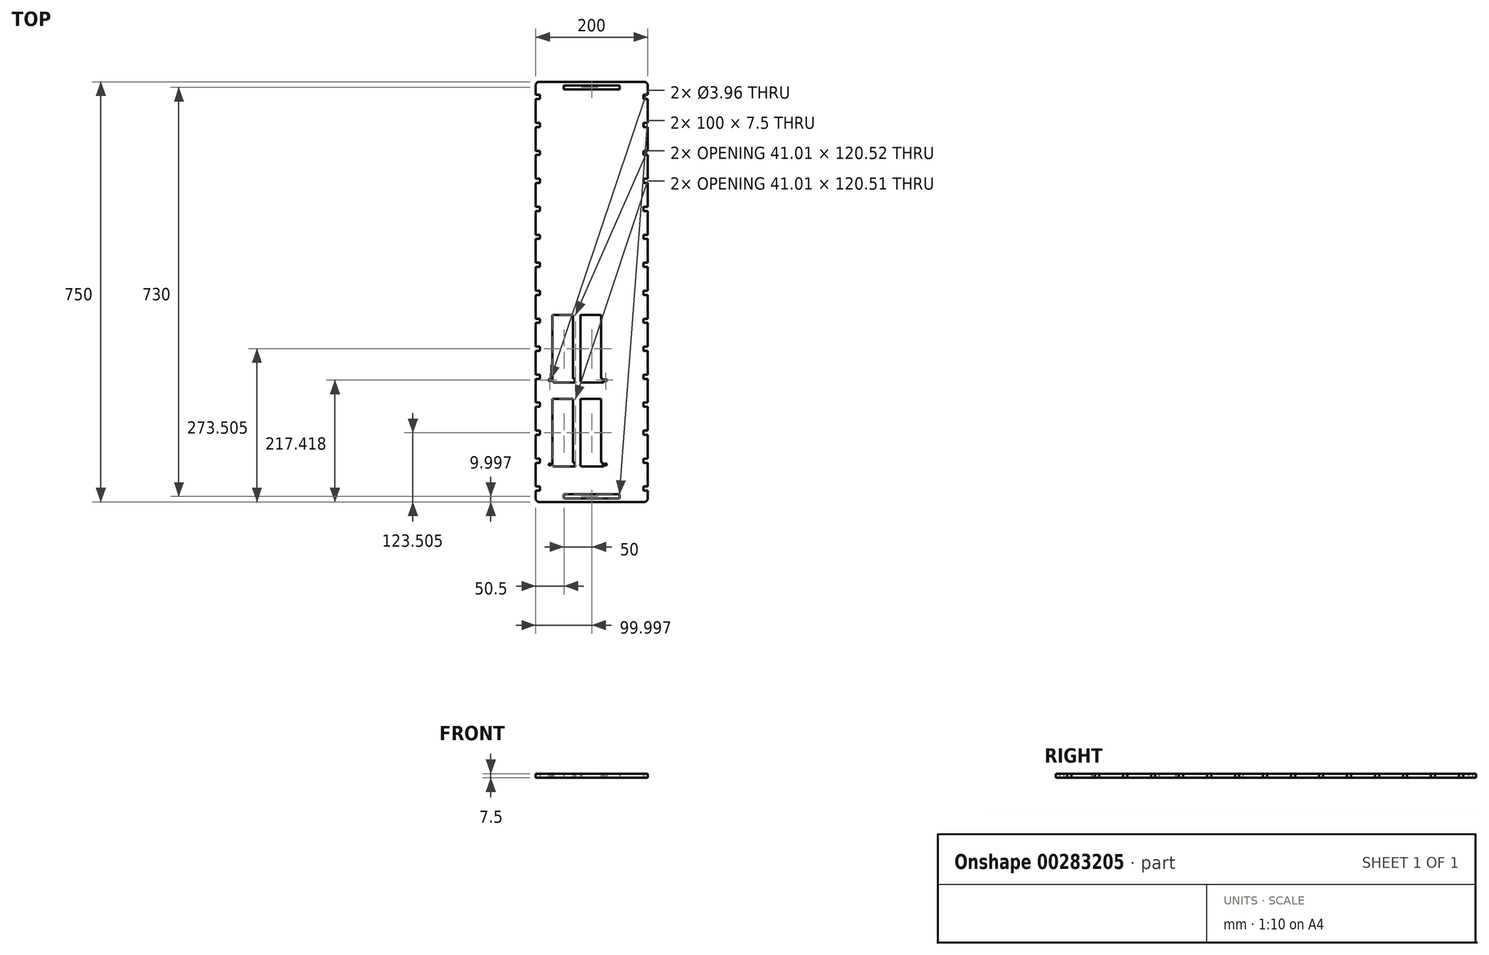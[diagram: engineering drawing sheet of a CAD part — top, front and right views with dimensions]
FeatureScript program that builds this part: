
annotation { "Feature Type Name" : "Feature", "Feature Type Description" : "" }
export const myFeature = defineFeature(function(context is Context, id is Id, definition is map)
    precondition{}
    {
        {
            var Q0;
            Q0=qCreatedBy(makeId("Top.planeOp"),FACE);
            var sketch = newSketch(context, id + "F0", { "sketchPlane" : qUnion([Q0])});
            skLineSegment(sketch, "E0.bottom", {"start": v(-77.83, 397.38) * mm, "end": v(109.47, 397.38) * mm});
            skLineSegment(sketch, "E0.top", {"start": v(-77.83, -352.62) * mm, "end": v(109.47, -352.62) * mm});
            skLineSegment(sketch, "E0.left", {"start": v(-84.18, 391.03) * mm, "end": v(-84.18, 374.07) * mm});
            skLineSegment(sketch, "E0.right", {"start": v(115.82, 391.03) * mm, "end": v(115.82, 374.18) * mm});
            skLineSegment(sketch, "E1", {"start": v(15.82, -352.62) * mm, "end": v(15.82, -332.62) * mm, "construction": true});
            skPoint(sketch, "E1.endSnap0", {"position": v(15.82, -352.62) * mm});
            skLineSegment(sketch, "E2", {"start": v(-84.18, 374.07) * mm, "end": v(-59.18, 374.07) * mm, "construction": true});
            skLineSegment(sketch, "E3", {"start": v(15.82, 397.38) * mm, "end": v(15.82, 377.38) * mm, "construction": true});
            skPoint(sketch, "E3.endSnap0", {"position": v(15.82, 397.38) * mm});
            skPoint(sketch, "E4.visualSharp", {"position": v(-84.18, 397.38) * mm});
            skArc(sketch, "E4.filletArc", {"start": v(-77.83, 397.38) * mm, "mid": v(-82.32, 395.52) * mm, "end": v(-84.18, 391.03) * mm});
            skPoint(sketch, "E5.visualSharp", {"position": v(115.82, 397.38) * mm});
            skArc(sketch, "E5.filletArc", {"start": v(115.82, 391.03) * mm, "mid": v(113.96, 395.52) * mm, "end": v(109.47, 397.38) * mm});
            skPoint(sketch, "E6.visualSharp", {"position": v(115.82, -352.62) * mm});
            skArc(sketch, "E6.filletArc", {"start": v(109.47, -352.62) * mm, "mid": v(113.96, -350.76) * mm, "end": v(115.82, -346.27) * mm});
            skPoint(sketch, "E7.visualSharp", {"position": v(-84.18, -352.62) * mm});
            skArc(sketch, "E7.filletArc", {"start": v(-84.18, -346.27) * mm, "mid": v(-82.32, -350.76) * mm, "end": v(-77.83, -352.62) * mm});
            skLineSegment(sketch, "E8.bottom", {"start": v(-84.18, -332.62) * mm, "end": v(-76.68, -332.62) * mm});
            skLineSegment(sketch, "E8.top", {"start": v(-84.18, -325.12) * mm, "end": v(-76.68, -325.12) * mm});
            skLineSegment(sketch, "E8.right", {"start": v(-76.68, -332.62) * mm, "end": v(-76.68, -325.12) * mm});
            skLineSegment(sketch, "E9.0.1.0", {"start": v(-84.18, -275.17) * mm, "end": v(-76.68, -275.17) * mm});
            skLineSegment(sketch, "E9.0.1.1", {"start": v(-84.18, -282.67) * mm, "end": v(-76.68, -282.67) * mm});
            skLineSegment(sketch, "E9.0.1.3", {"start": v(-76.68, -282.67) * mm, "end": v(-76.68, -275.17) * mm});
            skLineSegment(sketch, "E9.0.2.0", {"start": v(-84.18, -225.22) * mm, "end": v(-76.68, -225.22) * mm});
            skLineSegment(sketch, "E9.0.2.1", {"start": v(-84.18, -232.72) * mm, "end": v(-76.68, -232.72) * mm});
            skLineSegment(sketch, "E9.0.2.3", {"start": v(-76.68, -232.72) * mm, "end": v(-76.68, -225.22) * mm});
            skLineSegment(sketch, "E9.0.3.0", {"start": v(-84.18, -175.27) * mm, "end": v(-76.68, -175.27) * mm});
            skLineSegment(sketch, "E9.0.3.1", {"start": v(-84.18, -182.77) * mm, "end": v(-76.68, -182.77) * mm});
            skLineSegment(sketch, "E9.0.3.3", {"start": v(-76.68, -182.77) * mm, "end": v(-76.68, -175.27) * mm});
            skLineSegment(sketch, "E9.0.4.0", {"start": v(-84.18, -125.32) * mm, "end": v(-76.68, -125.32) * mm});
            skLineSegment(sketch, "E9.0.4.1", {"start": v(-84.18, -132.82) * mm, "end": v(-76.68, -132.82) * mm});
            skLineSegment(sketch, "E9.0.4.3", {"start": v(-76.68, -132.82) * mm, "end": v(-76.68, -125.32) * mm});
            skLineSegment(sketch, "E9.0.5.0", {"start": v(-84.18, -75.37) * mm, "end": v(-76.68, -75.37) * mm});
            skLineSegment(sketch, "E9.0.5.1", {"start": v(-84.18, -82.87) * mm, "end": v(-76.68, -82.87) * mm});
            skLineSegment(sketch, "E9.0.5.3", {"start": v(-76.68, -82.87) * mm, "end": v(-76.68, -75.37) * mm});
            skLineSegment(sketch, "E9.0.6.0", {"start": v(-84.18, -25.42) * mm, "end": v(-76.68, -25.42) * mm});
            skLineSegment(sketch, "E9.0.6.1", {"start": v(-84.18, -32.92) * mm, "end": v(-76.68, -32.92) * mm});
            skLineSegment(sketch, "E9.0.6.3", {"start": v(-76.68, -32.92) * mm, "end": v(-76.68, -25.42) * mm});
            skLineSegment(sketch, "E9.0.7.0", {"start": v(-84.18, 24.53) * mm, "end": v(-76.68, 24.53) * mm});
            skLineSegment(sketch, "E9.0.7.1", {"start": v(-84.18, 17.03) * mm, "end": v(-76.68, 17.03) * mm});
            skLineSegment(sketch, "E9.0.7.3", {"start": v(-76.68, 17.03) * mm, "end": v(-76.68, 24.53) * mm});
            skLineSegment(sketch, "E9.0.8.0", {"start": v(-84.18, 74.48) * mm, "end": v(-76.68, 74.48) * mm});
            skLineSegment(sketch, "E9.0.8.1", {"start": v(-84.18, 66.98) * mm, "end": v(-76.68, 66.98) * mm});
            skLineSegment(sketch, "E9.0.8.3", {"start": v(-76.68, 66.98) * mm, "end": v(-76.68, 74.48) * mm});
            skLineSegment(sketch, "E9.0.9.0", {"start": v(-84.18, 124.43) * mm, "end": v(-76.68, 124.43) * mm});
            skLineSegment(sketch, "E9.0.9.1", {"start": v(-84.18, 116.93) * mm, "end": v(-76.68, 116.93) * mm});
            skLineSegment(sketch, "E9.0.9.3", {"start": v(-76.68, 116.93) * mm, "end": v(-76.68, 124.43) * mm});
            skLineSegment(sketch, "E9.0.10.0", {"start": v(-84.18, 174.38) * mm, "end": v(-76.68, 174.38) * mm});
            skLineSegment(sketch, "E9.0.10.1", {"start": v(-84.18, 166.88) * mm, "end": v(-76.68, 166.88) * mm});
            skLineSegment(sketch, "E9.0.10.3", {"start": v(-76.68, 166.88) * mm, "end": v(-76.68, 174.38) * mm});
            skLineSegment(sketch, "E9.0.11.0", {"start": v(-84.18, 224.33) * mm, "end": v(-76.68, 224.33) * mm});
            skLineSegment(sketch, "E9.0.11.1", {"start": v(-84.18, 216.83) * mm, "end": v(-76.68, 216.83) * mm});
            skLineSegment(sketch, "E9.0.11.3", {"start": v(-76.68, 216.83) * mm, "end": v(-76.68, 224.33) * mm});
            skLineSegment(sketch, "E9.0.12.0", {"start": v(-84.18, 274.28) * mm, "end": v(-76.68, 274.28) * mm});
            skLineSegment(sketch, "E9.0.12.1", {"start": v(-84.18, 266.78) * mm, "end": v(-76.68, 266.78) * mm});
            skLineSegment(sketch, "E9.0.12.3", {"start": v(-76.68, 266.78) * mm, "end": v(-76.68, 274.28) * mm});
            skLineSegment(sketch, "E9.0.13.0", {"start": v(-84.18, 324.23) * mm, "end": v(-76.68, 324.23) * mm});
            skLineSegment(sketch, "E9.0.13.1", {"start": v(-84.18, 316.73) * mm, "end": v(-76.68, 316.73) * mm});
            skLineSegment(sketch, "E9.0.13.3", {"start": v(-76.68, 316.73) * mm, "end": v(-76.68, 324.23) * mm});
            skLineSegment(sketch, "E9.0.14.0", {"start": v(-84.18, 374.18) * mm, "end": v(-76.68, 374.18) * mm});
            skLineSegment(sketch, "E9.0.14.1", {"start": v(-84.18, 366.68) * mm, "end": v(-76.68, 366.68) * mm});
            skLineSegment(sketch, "E9.0.14.2", {"start": v(-84.18, 374.07) * mm, "end": v(-84.18, 374.18) * mm});
            skLineSegment(sketch, "E9.0.14.3", {"start": v(-76.68, 366.68) * mm, "end": v(-76.68, 374.18) * mm});
            skLineSegment(sketch, "E9.direction1", {"start": v(-84.18, -332.62) * mm, "end": v(-58.78, -332.62) * mm, "construction": true});
            skLineSegment(sketch, "E9.direction2", {"start": v(-84.18, -325.12) * mm, "end": v(-84.18, -282.67) * mm, "construction": true});
            skLineSegment(sketch, "E10.bottom", {"start": v(115.82, -332.62) * mm, "end": v(108.32, -332.62) * mm});
            skLineSegment(sketch, "E10.top", {"start": v(115.82, -325.12) * mm, "end": v(108.32, -325.12) * mm});
            skLineSegment(sketch, "E10.right", {"start": v(108.32, -332.62) * mm, "end": v(108.32, -325.12) * mm});
            skLineSegment(sketch, "E11.0.1.0", {"start": v(115.82, -282.67) * mm, "end": v(108.32, -282.67) * mm});
            skLineSegment(sketch, "E11.0.1.2", {"start": v(115.82, -275.17) * mm, "end": v(108.32, -275.17) * mm});
            skLineSegment(sketch, "E11.0.1.3", {"start": v(108.32, -282.67) * mm, "end": v(108.32, -275.17) * mm});
            skLineSegment(sketch, "E11.0.2.0", {"start": v(115.82, -232.72) * mm, "end": v(108.32, -232.72) * mm});
            skLineSegment(sketch, "E11.0.2.2", {"start": v(115.82, -225.22) * mm, "end": v(108.32, -225.22) * mm});
            skLineSegment(sketch, "E11.0.2.3", {"start": v(108.32, -232.72) * mm, "end": v(108.32, -225.22) * mm});
            skLineSegment(sketch, "E11.0.3.0", {"start": v(115.82, -182.77) * mm, "end": v(108.32, -182.77) * mm});
            skLineSegment(sketch, "E11.0.3.2", {"start": v(115.82, -175.27) * mm, "end": v(108.32, -175.27) * mm});
            skLineSegment(sketch, "E11.0.3.3", {"start": v(108.32, -182.77) * mm, "end": v(108.32, -175.27) * mm});
            skLineSegment(sketch, "E11.0.4.0", {"start": v(115.82, -132.82) * mm, "end": v(108.32, -132.82) * mm});
            skLineSegment(sketch, "E11.0.4.2", {"start": v(115.82, -125.32) * mm, "end": v(108.32, -125.32) * mm});
            skLineSegment(sketch, "E11.0.4.3", {"start": v(108.32, -132.82) * mm, "end": v(108.32, -125.32) * mm});
            skLineSegment(sketch, "E11.0.5.0", {"start": v(115.82, -82.87) * mm, "end": v(108.32, -82.87) * mm});
            skLineSegment(sketch, "E11.0.5.2", {"start": v(115.82, -75.37) * mm, "end": v(108.32, -75.37) * mm});
            skLineSegment(sketch, "E11.0.5.3", {"start": v(108.32, -82.87) * mm, "end": v(108.32, -75.37) * mm});
            skLineSegment(sketch, "E11.0.6.0", {"start": v(115.82, -32.92) * mm, "end": v(108.32, -32.92) * mm});
            skLineSegment(sketch, "E11.0.6.2", {"start": v(115.82, -25.42) * mm, "end": v(108.32, -25.42) * mm});
            skLineSegment(sketch, "E11.0.6.3", {"start": v(108.32, -32.92) * mm, "end": v(108.32, -25.42) * mm});
            skLineSegment(sketch, "E11.0.7.0", {"start": v(115.82, 17.03) * mm, "end": v(108.32, 17.03) * mm});
            skLineSegment(sketch, "E11.0.7.2", {"start": v(115.82, 24.53) * mm, "end": v(108.32, 24.53) * mm});
            skLineSegment(sketch, "E11.0.7.3", {"start": v(108.32, 17.03) * mm, "end": v(108.32, 24.53) * mm});
            skLineSegment(sketch, "E11.0.8.0", {"start": v(115.82, 66.98) * mm, "end": v(108.32, 66.98) * mm});
            skLineSegment(sketch, "E11.0.8.2", {"start": v(115.82, 74.48) * mm, "end": v(108.32, 74.48) * mm});
            skLineSegment(sketch, "E11.0.8.3", {"start": v(108.32, 66.98) * mm, "end": v(108.32, 74.48) * mm});
            skLineSegment(sketch, "E11.0.9.0", {"start": v(115.82, 116.93) * mm, "end": v(108.32, 116.93) * mm});
            skLineSegment(sketch, "E11.0.9.2", {"start": v(115.82, 124.43) * mm, "end": v(108.32, 124.43) * mm});
            skLineSegment(sketch, "E11.0.9.3", {"start": v(108.32, 116.93) * mm, "end": v(108.32, 124.43) * mm});
            skLineSegment(sketch, "E11.0.10.0", {"start": v(115.82, 166.88) * mm, "end": v(108.32, 166.88) * mm});
            skLineSegment(sketch, "E11.0.10.2", {"start": v(115.82, 174.38) * mm, "end": v(108.32, 174.38) * mm});
            skLineSegment(sketch, "E11.0.10.3", {"start": v(108.32, 166.88) * mm, "end": v(108.32, 174.38) * mm});
            skLineSegment(sketch, "E11.0.11.0", {"start": v(115.82, 216.83) * mm, "end": v(108.32, 216.83) * mm});
            skLineSegment(sketch, "E11.0.11.2", {"start": v(115.82, 224.33) * mm, "end": v(108.32, 224.33) * mm});
            skLineSegment(sketch, "E11.0.11.3", {"start": v(108.32, 216.83) * mm, "end": v(108.32, 224.33) * mm});
            skLineSegment(sketch, "E11.0.12.0", {"start": v(115.82, 266.78) * mm, "end": v(108.32, 266.78) * mm});
            skLineSegment(sketch, "E11.0.12.2", {"start": v(115.82, 274.28) * mm, "end": v(108.32, 274.28) * mm});
            skLineSegment(sketch, "E11.0.12.3", {"start": v(108.32, 266.78) * mm, "end": v(108.32, 274.28) * mm});
            skLineSegment(sketch, "E11.0.13.0", {"start": v(115.82, 316.73) * mm, "end": v(108.32, 316.73) * mm});
            skLineSegment(sketch, "E11.0.13.2", {"start": v(115.82, 324.23) * mm, "end": v(108.32, 324.23) * mm});
            skLineSegment(sketch, "E11.0.13.3", {"start": v(108.32, 316.73) * mm, "end": v(108.32, 324.23) * mm});
            skLineSegment(sketch, "E11.0.14.0", {"start": v(115.82, 366.68) * mm, "end": v(108.32, 366.68) * mm});
            skLineSegment(sketch, "E11.0.14.2", {"start": v(115.82, 374.18) * mm, "end": v(108.32, 374.18) * mm});
            skLineSegment(sketch, "E11.0.14.3", {"start": v(108.32, 366.68) * mm, "end": v(108.32, 374.18) * mm});
            skLineSegment(sketch, "E11.direction1", {"start": v(108.32, -332.62) * mm, "end": v(133.72, -332.62) * mm, "construction": true});
            skLineSegment(sketch, "E11.direction2", {"start": v(108.32, -332.62) * mm, "end": v(108.32, -282.67) * mm, "construction": true});
            skPoint(sketch, "E12.middle", {"position": v(-44.98, -226.9) * mm});
            skLineSegment(sketch, "E13.bottom", {"start": v(-41.79, -168.86) * mm, "end": v(-48.16, -168.86) * mm});
            skLineSegment(sketch, "E13.left", {"start": v(-35.77, -180.24) * mm, "end": v(-35.77, -284.94) * mm, "construction": true});
            skLineSegment(sketch, "E13.right", {"start": v(-54.18, -180.24) * mm, "end": v(-54.18, -282.4) * mm});
            skLineSegment(sketch, "E14.right", {"start": v(-39.88, -170.76) * mm, "end": v(-39.88, -176.12) * mm, "construction": true});
            skLineSegment(sketch, "E15.MirrorCS", {"start": v(-50.07, -170.76) * mm, "end": v(-50.07, -176.12) * mm, "construction": true});
            skLineSegment(sketch, "E16", {"start": v(-35.77, -180.24) * mm, "end": v(-39.88, -176.12) * mm, "construction": true});
            skLineSegment(sketch, "E17.MirrorCS", {"start": v(-54.18, -180.24) * mm, "end": v(-50.07, -176.12) * mm, "construction": true});
            skPoint(sketch, "E18.MirrorCS.end.orphan", {"position": v(-54.18, -180.24) * mm});
            skArc(sketch, "E19.filletArc", {"start": v(-39.88, -170.76) * mm, "mid": v(-40.44, -169.42) * mm, "end": v(-41.79, -168.86) * mm, "construction": true});
            skArc(sketch, "E20.filletArc", {"start": v(-48.16, -168.86) * mm, "mid": v(-49.5, -169.42) * mm, "end": v(-50.07, -170.76) * mm, "construction": true});
            skLineSegment(sketch, "E21", {"start": v(-51.64, -284.94) * mm, "end": v(-54.18, -282.4) * mm});
            skLineSegment(sketch, "E22.left", {"start": v(-51.64, -284.94) * mm, "end": v(-51.64, -288) * mm});
            skLineSegment(sketch, "E22.right", {"start": v(-32.6, -286.59) * mm, "end": v(-32.6, -288) * mm, "construction": true});
            skLineSegment(sketch, "E23", {"start": v(-34.24, -284.94) * mm, "end": v(-32.6, -286.59) * mm, "construction": true});
            skLineSegment(sketch, "E24.bottom", {"start": v(-51.64, -288) * mm, "end": v(-32.6, -288) * mm});
            skLineSegment(sketch, "E24.top", {"start": v(-51.64, -288.87) * mm, "end": v(-32.6, -288.87) * mm});
            skLineSegment(sketch, "E24.left", {"start": v(-51.64, -288) * mm, "end": v(-51.64, -288.87) * mm});
            skLineSegment(sketch, "E24.right", {"start": v(-32.6, -288) * mm, "end": v(-32.6, -288.87) * mm, "construction": true});
            skLineSegment(sketch, "E25.bottom", {"start": v(65.82, -346.37) * mm, "end": v(-34.18, -346.37) * mm});
            skLineSegment(sketch, "E25.top", {"start": v(65.82, -338.87) * mm, "end": v(-34.18, -338.87) * mm});
            skLineSegment(sketch, "E25.left", {"start": v(65.82, -346.37) * mm, "end": v(65.82, -338.87) * mm});
            skLineSegment(sketch, "E25.right", {"start": v(-34.18, -346.37) * mm, "end": v(-34.18, -338.87) * mm});
            skPoint(sketch, "E25.middle", {"position": v(15.82, -342.62) * mm});
            skLineSegment(sketch, "E26.bottom", {"start": v(65.82, 383.63) * mm, "end": v(-34.18, 383.63) * mm});
            skLineSegment(sketch, "E26.top", {"start": v(65.82, 391.13) * mm, "end": v(-34.18, 391.13) * mm});
            skLineSegment(sketch, "E26.left", {"start": v(65.82, 383.63) * mm, "end": v(65.82, 391.13) * mm});
            skLineSegment(sketch, "E26.right", {"start": v(-34.18, 383.63) * mm, "end": v(-34.18, 391.13) * mm});
            skPoint(sketch, "E26.middle", {"position": v(15.82, 387.38) * mm});
            skLineSegment(sketch, "E27", {"start": v(-15.18, -338.87) * mm, "end": v(-15.18, -288.87) * mm, "construction": true});
            skLineSegment(sketch, "E28", {"start": v(115.82, -321) * mm, "end": v(100.82, -321) * mm, "construction": true});
            skLineSegment(sketch, "E29.bottom", {"start": v(100.82, -288.87) * mm, "end": v(40.82, -288.87) * mm, "construction": true});
            skLineSegment(sketch, "E29.top", {"start": v(100.82, 51.49) * mm, "end": v(40.82, 51.49) * mm, "construction": true});
            skLineSegment(sketch, "E29.left", {"start": v(100.82, -288.87) * mm, "end": v(100.82, 51.49) * mm, "construction": true});
            skLineSegment(sketch, "E29.right", {"start": v(40.82, -288.87) * mm, "end": v(40.82, 51.49) * mm, "construction": true});
            skPoint(sketch, "E30.0.1.0", {"position": v(-44.98, -76.9) * mm});
            skLineSegment(sketch, "E30.0.1.1", {"start": v(-51.64, -138.87) * mm, "end": v(-32.6, -138.87) * mm});
            skLineSegment(sketch, "E30.0.1.3", {"start": v(-51.64, -138) * mm, "end": v(-32.6, -138) * mm});
            skPoint(sketch, "E30.0.1.4", {"position": v(-54.18, -30.24) * mm});
            skLineSegment(sketch, "E30.0.1.5", {"start": v(-54.18, -30.24) * mm, "end": v(-54.18, -132.4) * mm});
            skLineSegment(sketch, "E30.0.1.6", {"start": v(-35.77, -30.24) * mm, "end": v(-35.77, -134.94) * mm, "construction": true});
            skPoint(sketch, "E30.0.1.7", {"position": v(-44.98, -76.9) * mm});
            skLineSegment(sketch, "E30.0.1.8", {"start": v(-51.64, -138) * mm, "end": v(-32.6, -138) * mm});
            skLineSegment(sketch, "E30.0.1.9", {"start": v(-35.77, -134.94) * mm, "end": v(-51.64, -134.94) * mm});
            skArc(sketch, "E30.0.1.10", {"start": v(-39.88, -20.76) * mm, "mid": v(-40.44, -19.42) * mm, "end": v(-41.79, -18.86) * mm, "construction": true});
            skLineSegment(sketch, "E30.0.1.11", {"start": v(-35.77, -30.24) * mm, "end": v(-39.88, -26.12) * mm, "construction": true});
            skLineSegment(sketch, "E30.0.1.12", {"start": v(-41.79, -18.86) * mm, "end": v(-48.16, -18.86) * mm});
            skLineSegment(sketch, "E30.0.1.13", {"start": v(-39.88, -20.76) * mm, "end": v(-39.88, -26.12) * mm, "construction": true});
            skLineSegment(sketch, "E30.0.1.14", {"start": v(-54.18, -30.24) * mm, "end": v(-50.07, -26.12) * mm, "construction": true});
            skArc(sketch, "E30.0.1.15", {"start": v(-48.16, -18.86) * mm, "mid": v(-49.5, -19.42) * mm, "end": v(-50.07, -20.76) * mm, "construction": true});
            skLineSegment(sketch, "E30.0.1.16", {"start": v(-50.07, -20.76) * mm, "end": v(-50.07, -26.12) * mm, "construction": true});
            skLineSegment(sketch, "E30.0.1.17", {"start": v(-51.64, -134.94) * mm, "end": v(-54.18, -132.4) * mm});
            skLineSegment(sketch, "E30.0.1.18", {"start": v(-51.64, -134.94) * mm, "end": v(-51.64, -138) * mm});
            skLineSegment(sketch, "E30.0.1.19", {"start": v(-51.64, -138) * mm, "end": v(-51.64, -138.87) * mm});
            skLineSegment(sketch, "E30.0.1.20", {"start": v(-34.24, -134.94) * mm, "end": v(-32.6, -136.59) * mm, "construction": true});
            skLineSegment(sketch, "E30.0.1.21", {"start": v(-32.6, -138) * mm, "end": v(-32.6, -138.87) * mm, "construction": true});
            skLineSegment(sketch, "E30.0.1.22", {"start": v(-32.6, -136.59) * mm, "end": v(-32.6, -138) * mm, "construction": true});
            skPoint(sketch, "E30.1.0.0", {"position": v(-26.56, -226.9) * mm});
            skLineSegment(sketch, "E30.1.0.1", {"start": v(-33.23, -288.87) * mm, "end": v(-14.18, -288.87) * mm});
            skLineSegment(sketch, "E30.1.0.2", {"start": v(-33.23, -284.94) * mm, "end": v(-15.83, -284.94) * mm});
            skPoint(sketch, "E30.1.0.4", {"position": v(-35.77, -180.24) * mm});
            skLineSegment(sketch, "E30.1.0.5", {"start": v(-35.77, -180.24) * mm, "end": v(-35.77, -282.4) * mm, "construction": true});
            skLineSegment(sketch, "E30.1.0.6", {"start": v(-17.35, -180.24) * mm, "end": v(-17.35, -284.94) * mm});
            skPoint(sketch, "E30.1.0.7", {"position": v(-26.56, -226.9) * mm});
            skLineSegment(sketch, "E30.1.0.8", {"start": v(-33.23, -288) * mm, "end": v(-14.18, -288) * mm});
            skArc(sketch, "E30.1.0.10", {"start": v(-21.47, -170.76) * mm, "mid": v(-22.03, -169.42) * mm, "end": v(-23.37, -168.86) * mm, "construction": true});
            skLineSegment(sketch, "E30.1.0.11", {"start": v(-17.35, -180.24) * mm, "end": v(-21.47, -176.12) * mm, "construction": true});
            skLineSegment(sketch, "E30.1.0.12", {"start": v(-23.37, -168.86) * mm, "end": v(-29.75, -168.86) * mm});
            skLineSegment(sketch, "E30.1.0.13", {"start": v(-21.47, -170.76) * mm, "end": v(-21.47, -176.12) * mm, "construction": true});
            skLineSegment(sketch, "E30.1.0.14", {"start": v(-35.77, -180.24) * mm, "end": v(-31.65, -176.12) * mm, "construction": true});
            skArc(sketch, "E30.1.0.15", {"start": v(-29.75, -168.86) * mm, "mid": v(-31.1, -169.42) * mm, "end": v(-31.65, -170.76) * mm, "construction": true});
            skLineSegment(sketch, "E30.1.0.16", {"start": v(-31.65, -170.76) * mm, "end": v(-31.65, -176.12) * mm, "construction": true});
            skLineSegment(sketch, "E30.1.0.17", {"start": v(-33.23, -284.94) * mm, "end": v(-35.77, -282.4) * mm, "construction": true});
            skLineSegment(sketch, "E30.1.0.18", {"start": v(-33.23, -284.94) * mm, "end": v(-33.23, -288) * mm, "construction": true});
            skLineSegment(sketch, "E30.1.0.19", {"start": v(-33.23, -288) * mm, "end": v(-33.23, -288.87) * mm, "construction": true});
            skLineSegment(sketch, "E30.1.0.20", {"start": v(-15.83, -284.94) * mm, "end": v(-14.18, -286.59) * mm, "construction": true});
            skLineSegment(sketch, "E30.1.0.21", {"start": v(-14.18, -288) * mm, "end": v(-14.18, -288.87) * mm});
            skLineSegment(sketch, "E30.1.0.22", {"start": v(-14.18, -286.59) * mm, "end": v(-14.18, -288) * mm});
            skPoint(sketch, "E30.1.1.0", {"position": v(-26.56, -76.9) * mm});
            skLineSegment(sketch, "E30.1.1.1", {"start": v(-33.23, -138.87) * mm, "end": v(-14.18, -138.87) * mm});
            skLineSegment(sketch, "E30.1.1.3", {"start": v(-33.23, -138) * mm, "end": v(-14.18, -138) * mm});
            skPoint(sketch, "E30.1.1.4", {"position": v(-35.77, -30.24) * mm});
            skLineSegment(sketch, "E30.1.1.5", {"start": v(-35.77, -30.24) * mm, "end": v(-35.77, -132.4) * mm, "construction": true});
            skLineSegment(sketch, "E30.1.1.6", {"start": v(-17.35, -30.24) * mm, "end": v(-17.35, -134.94) * mm});
            skPoint(sketch, "E30.1.1.7", {"position": v(-26.56, -76.9) * mm});
            skLineSegment(sketch, "E30.1.1.8", {"start": v(-33.23, -138) * mm, "end": v(-14.18, -138) * mm});
            skLineSegment(sketch, "E30.1.1.9", {"start": v(-17.35, -134.94) * mm, "end": v(-33.23, -134.94) * mm});
            skArc(sketch, "E30.1.1.10", {"start": v(-21.47, -20.76) * mm, "mid": v(-22.03, -19.42) * mm, "end": v(-23.37, -18.86) * mm, "construction": true});
            skLineSegment(sketch, "E30.1.1.11", {"start": v(-17.35, -30.24) * mm, "end": v(-21.47, -26.12) * mm, "construction": true});
            skLineSegment(sketch, "E30.1.1.12", {"start": v(-23.37, -18.86) * mm, "end": v(-29.75, -18.86) * mm});
            skLineSegment(sketch, "E30.1.1.13", {"start": v(-21.47, -20.76) * mm, "end": v(-21.47, -26.12) * mm, "construction": true});
            skLineSegment(sketch, "E30.1.1.14", {"start": v(-35.77, -30.24) * mm, "end": v(-31.65, -26.12) * mm, "construction": true});
            skArc(sketch, "E30.1.1.15", {"start": v(-29.75, -18.86) * mm, "mid": v(-31.1, -19.42) * mm, "end": v(-31.65, -20.76) * mm, "construction": true});
            skLineSegment(sketch, "E30.1.1.16", {"start": v(-31.65, -20.76) * mm, "end": v(-31.65, -26.12) * mm, "construction": true});
            skLineSegment(sketch, "E30.1.1.17", {"start": v(-33.23, -134.94) * mm, "end": v(-35.77, -132.4) * mm, "construction": true});
            skLineSegment(sketch, "E30.1.1.18", {"start": v(-33.23, -134.94) * mm, "end": v(-33.23, -138) * mm, "construction": true});
            skLineSegment(sketch, "E30.1.1.19", {"start": v(-33.23, -138) * mm, "end": v(-33.23, -138.87) * mm, "construction": true});
            skLineSegment(sketch, "E30.1.1.20", {"start": v(-15.83, -134.94) * mm, "end": v(-14.18, -136.59) * mm, "construction": true});
            skLineSegment(sketch, "E30.1.1.21", {"start": v(-14.18, -138) * mm, "end": v(-14.18, -138.87) * mm});
            skLineSegment(sketch, "E30.1.1.22", {"start": v(-14.18, -136.59) * mm, "end": v(-14.18, -138) * mm});
            skLineSegment(sketch, "E31.1.0.1", {"start": v(32.65, -30.24) * mm, "end": v(32.65, -134.94) * mm});
            skLineSegment(sketch, "E31.1.0.2", {"start": v(14.23, -134.94) * mm, "end": v(-1.64, -134.94) * mm});
            skPoint(sketch, "E31.1.0.3", {"position": v(5.02, -76.9) * mm});
            skLineSegment(sketch, "E31.1.0.4", {"start": v(14.23, -30.24) * mm, "end": v(14.23, -134.94) * mm, "construction": true});
            skLineSegment(sketch, "E31.1.0.5", {"start": v(16.77, -138.87) * mm, "end": v(35.82, -138.87) * mm});
            skLineSegment(sketch, "E31.1.0.6", {"start": v(-1.64, -138.87) * mm, "end": v(17.4, -138.87) * mm});
            skPoint(sketch, "E31.1.0.7", {"position": v(23.44, -76.9) * mm});
            skPoint(sketch, "E31.1.0.8", {"position": v(-4.18, -30.24) * mm});
            skLineSegment(sketch, "E31.1.0.9", {"start": v(-1.64, -138) * mm, "end": v(17.4, -138) * mm});
            skLineSegment(sketch, "E31.1.0.10", {"start": v(-4.18, -30.24) * mm, "end": v(-4.18, -132.4) * mm});
            skPoint(sketch, "E31.1.0.11", {"position": v(14.23, -30.24) * mm});
            skPoint(sketch, "E31.1.0.13", {"position": v(23.44, -76.9) * mm});
            skPoint(sketch, "E31.1.0.14", {"position": v(5.02, -76.9) * mm});
            skLineSegment(sketch, "E31.1.0.16", {"start": v(32.65, -134.94) * mm, "end": v(16.77, -134.94) * mm});
            skLineSegment(sketch, "E31.1.0.17", {"start": v(14.23, -30.24) * mm, "end": v(14.23, -132.4) * mm, "construction": true});
            skLineSegment(sketch, "E31.1.0.19", {"start": v(28.53, -20.76) * mm, "end": v(28.53, -26.12) * mm, "construction": true});
            skArc(sketch, "E31.1.0.20", {"start": v(10.12, -20.76) * mm, "mid": v(9.56, -19.42) * mm, "end": v(8.21, -18.86) * mm, "construction": true});
            skArc(sketch, "E31.1.0.21", {"start": v(28.53, -20.76) * mm, "mid": v(27.97, -19.42) * mm, "end": v(26.63, -18.86) * mm, "construction": true});
            skLineSegment(sketch, "E31.1.0.22", {"start": v(18.35, -20.76) * mm, "end": v(18.35, -26.12) * mm, "construction": true});
            skLineSegment(sketch, "E31.1.0.23", {"start": v(8.21, -18.86) * mm, "end": v(1.84, -18.86) * mm});
            skArc(sketch, "E31.1.0.24", {"start": v(20.25, -18.86) * mm, "mid": v(18.9, -19.42) * mm, "end": v(18.35, -20.76) * mm, "construction": true});
            skLineSegment(sketch, "E31.1.0.25", {"start": v(16.77, -138) * mm, "end": v(35.82, -138) * mm});
            skLineSegment(sketch, "E31.1.0.26", {"start": v(32.65, -30.24) * mm, "end": v(28.53, -26.12) * mm, "construction": true});
            skLineSegment(sketch, "E31.1.0.27", {"start": v(26.63, -18.86) * mm, "end": v(20.25, -18.86) * mm});
            skLineSegment(sketch, "E31.1.0.28", {"start": v(-4.18, -30.24) * mm, "end": v(-0.07, -26.12) * mm, "construction": true});
            skLineSegment(sketch, "E31.1.0.29", {"start": v(10.12, -20.76) * mm, "end": v(10.12, -26.12) * mm, "construction": true});
            skLineSegment(sketch, "E31.1.0.30", {"start": v(-0.07, -20.76) * mm, "end": v(-0.07, -26.12) * mm, "construction": true});
            skArc(sketch, "E31.1.0.31", {"start": v(1.84, -18.86) * mm, "mid": v(0.5, -19.42) * mm, "end": v(-0.07, -20.76) * mm, "construction": true});
            skLineSegment(sketch, "E31.1.0.32", {"start": v(34.17, -134.94) * mm, "end": v(35.82, -136.59) * mm, "construction": true});
            skLineSegment(sketch, "E31.1.0.33", {"start": v(-1.64, -138) * mm, "end": v(-1.64, -138.87) * mm});
            skLineSegment(sketch, "E31.1.0.34", {"start": v(35.82, -138) * mm, "end": v(35.82, -138.87) * mm});
            skLineSegment(sketch, "E31.1.0.35", {"start": v(-1.64, -134.94) * mm, "end": v(-4.18, -132.4) * mm});
            skLineSegment(sketch, "E31.1.0.36", {"start": v(35.82, -136.59) * mm, "end": v(35.82, -138) * mm});
            skLineSegment(sketch, "E31.1.0.37", {"start": v(-1.64, -134.94) * mm, "end": v(-1.64, -138) * mm});
            skLineSegment(sketch, "E31.1.0.38", {"start": v(14.23, -30.24) * mm, "end": v(10.12, -26.12) * mm, "construction": true});
            skLineSegment(sketch, "E31.1.0.39", {"start": v(14.23, -30.24) * mm, "end": v(18.35, -26.12) * mm, "construction": true});
            skLineSegment(sketch, "E31.1.0.40", {"start": v(16.77, -134.94) * mm, "end": v(16.77, -138) * mm, "construction": true});
            skLineSegment(sketch, "E31.1.0.41", {"start": v(16.77, -134.94) * mm, "end": v(14.23, -132.4) * mm, "construction": true});
            skLineSegment(sketch, "E31.1.0.42", {"start": v(16.77, -138) * mm, "end": v(16.77, -138.87) * mm, "construction": true});
            skLineSegment(sketch, "E31.1.0.43", {"start": v(17.4, -136.59) * mm, "end": v(17.4, -138) * mm, "construction": true});
            skLineSegment(sketch, "E31.1.0.44", {"start": v(15.76, -134.94) * mm, "end": v(17.4, -136.59) * mm, "construction": true});
            skLineSegment(sketch, "E31.1.0.45", {"start": v(17.4, -138) * mm, "end": v(17.4, -138.87) * mm, "construction": true});
            skLineSegment(sketch, "E31.1.0.47", {"start": v(-1.64, -284.94) * mm, "end": v(15.76, -284.94) * mm});
            skLineSegment(sketch, "E31.1.0.49", {"start": v(14.23, -180.24) * mm, "end": v(14.23, -282.4) * mm, "construction": true});
            skPoint(sketch, "E31.1.0.50", {"position": v(5.02, -226.9) * mm});
            skPoint(sketch, "E31.1.0.51", {"position": v(14.23, -180.24) * mm});
            skLineSegment(sketch, "E31.1.0.52", {"start": v(16.77, -288.87) * mm, "end": v(35.82, -288.87) * mm});
            skPoint(sketch, "E31.1.0.53", {"position": v(23.44, -226.9) * mm});
            skLineSegment(sketch, "E31.1.0.54", {"start": v(32.65, -180.24) * mm, "end": v(32.65, -284.94) * mm});
            skLineSegment(sketch, "E31.1.0.55", {"start": v(16.77, -284.94) * mm, "end": v(34.17, -284.94) * mm});
            skPoint(sketch, "E31.1.0.57", {"position": v(-4.18, -180.24) * mm});
            skLineSegment(sketch, "E31.1.0.58", {"start": v(-4.18, -180.24) * mm, "end": v(-4.18, -282.4) * mm});
            skLineSegment(sketch, "E31.1.0.60", {"start": v(16.77, -288) * mm, "end": v(35.82, -288) * mm});
            skLineSegment(sketch, "E31.1.0.61", {"start": v(14.23, -180.24) * mm, "end": v(14.23, -284.94) * mm, "construction": true});
            skLineSegment(sketch, "E31.1.0.62", {"start": v(-1.64, -288) * mm, "end": v(17.4, -288) * mm});
            skPoint(sketch, "E31.1.0.64", {"position": v(23.44, -226.9) * mm});
            skPoint(sketch, "E31.1.0.65", {"position": v(5.02, -226.9) * mm});
            skLineSegment(sketch, "E31.1.0.66", {"start": v(-1.64, -288.87) * mm, "end": v(16.77, -288.87) * mm});
            skLineSegment(sketch, "E31.1.0.67", {"start": v(10.12, -170.76) * mm, "end": v(10.12, -176.12) * mm, "construction": true});
            skArc(sketch, "E31.1.0.68", {"start": v(28.53, -170.76) * mm, "mid": v(27.97, -169.42) * mm, "end": v(26.63, -168.86) * mm, "construction": true});
            skArc(sketch, "E31.1.0.69", {"start": v(10.12, -170.76) * mm, "mid": v(9.56, -169.42) * mm, "end": v(8.21, -168.86) * mm, "construction": true});
            skLineSegment(sketch, "E31.1.0.70", {"start": v(26.63, -168.86) * mm, "end": v(20.25, -168.86) * mm});
            skLineSegment(sketch, "E31.1.0.71", {"start": v(8.21, -168.86) * mm, "end": v(1.84, -168.86) * mm});
            skLineSegment(sketch, "E31.1.0.72", {"start": v(28.53, -170.76) * mm, "end": v(28.53, -176.12) * mm, "construction": true});
            skLineSegment(sketch, "E31.1.0.73", {"start": v(32.65, -180.24) * mm, "end": v(28.53, -176.12) * mm, "construction": true});
            skArc(sketch, "E31.1.0.74", {"start": v(20.25, -168.86) * mm, "mid": v(18.9, -169.42) * mm, "end": v(18.35, -170.76) * mm, "construction": true});
            skLineSegment(sketch, "E31.1.0.75", {"start": v(18.35, -170.76) * mm, "end": v(18.35, -176.12) * mm, "construction": true});
            skLineSegment(sketch, "E31.1.0.76", {"start": v(-4.18, -180.24) * mm, "end": v(-0.07, -176.12) * mm, "construction": true});
            skArc(sketch, "E31.1.0.77", {"start": v(1.84, -168.86) * mm, "mid": v(0.5, -169.42) * mm, "end": v(-0.07, -170.76) * mm, "construction": true});
            skLineSegment(sketch, "E31.1.0.78", {"start": v(-0.07, -170.76) * mm, "end": v(-0.07, -176.12) * mm, "construction": true});
            skLineSegment(sketch, "E31.1.0.79", {"start": v(14.23, -180.24) * mm, "end": v(18.35, -176.12) * mm, "construction": true});
            skLineSegment(sketch, "E31.1.0.80", {"start": v(35.82, -286.59) * mm, "end": v(35.82, -288) * mm});
            skLineSegment(sketch, "E31.1.0.81", {"start": v(-1.64, -284.94) * mm, "end": v(-4.18, -282.4) * mm});
            skLineSegment(sketch, "E31.1.0.82", {"start": v(35.82, -288) * mm, "end": v(35.82, -288.87) * mm});
            skLineSegment(sketch, "E31.1.0.83", {"start": v(34.17, -284.94) * mm, "end": v(35.82, -286.59) * mm, "construction": true});
            skLineSegment(sketch, "E31.1.0.84", {"start": v(16.77, -284.94) * mm, "end": v(14.23, -282.4) * mm, "construction": true});
            skLineSegment(sketch, "E31.1.0.85", {"start": v(-1.64, -288) * mm, "end": v(-1.64, -288.87) * mm});
            skLineSegment(sketch, "E31.1.0.86", {"start": v(14.23, -180.24) * mm, "end": v(10.12, -176.12) * mm, "construction": true});
            skLineSegment(sketch, "E31.1.0.87", {"start": v(-1.64, -284.94) * mm, "end": v(-1.64, -288) * mm});
            skLineSegment(sketch, "E31.1.0.88", {"start": v(15.76, -284.94) * mm, "end": v(17.4, -286.59) * mm, "construction": true});
            skLineSegment(sketch, "E31.1.0.89", {"start": v(16.77, -284.94) * mm, "end": v(16.77, -288) * mm, "construction": true});
            skLineSegment(sketch, "E31.1.0.90", {"start": v(17.4, -288) * mm, "end": v(17.4, -288.87) * mm, "construction": true});
            skLineSegment(sketch, "E31.1.0.91", {"start": v(16.77, -288) * mm, "end": v(16.77, -288.87) * mm, "construction": true});
            skLineSegment(sketch, "E31.1.0.92", {"start": v(17.4, -286.59) * mm, "end": v(17.4, -288) * mm, "construction": true});
            skLineSegment(sketch, "E32", {"start": v(-54.18, -30.24) * mm, "end": v(-54.18, -18.86) * mm});
            skLineSegment(sketch, "E33", {"start": v(-54.18, -18.86) * mm, "end": v(-48.16, -18.86) * mm});
            skLineSegment(sketch, "E34", {"start": v(-41.79, -18.86) * mm, "end": v(-29.75, -18.86) * mm});
            skLineSegment(sketch, "E35", {"start": v(-23.37, -18.86) * mm, "end": v(-17.35, -18.86) * mm});
            skLineSegment(sketch, "E36", {"start": v(-17.35, -18.86) * mm, "end": v(-17.35, -30.24) * mm});
            skLineSegment(sketch, "E37", {"start": v(-4.18, -30.24) * mm, "end": v(-4.18, -18.86) * mm});
            skLineSegment(sketch, "E38", {"start": v(-4.18, -18.86) * mm, "end": v(1.84, -18.86) * mm});
            skLineSegment(sketch, "E39", {"start": v(8.21, -18.86) * mm, "end": v(20.25, -18.86) * mm});
            skLineSegment(sketch, "E40", {"start": v(26.63, -18.86) * mm, "end": v(32.65, -18.86) * mm});
            skLineSegment(sketch, "E41", {"start": v(32.65, -18.86) * mm, "end": v(32.65, -30.24) * mm});
            skLineSegment(sketch, "E42", {"start": v(-54.18, -180.24) * mm, "end": v(-54.18, -168.86) * mm});
            skLineSegment(sketch, "E43", {"start": v(-54.18, -168.86) * mm, "end": v(-48.16, -168.86) * mm});
            skLineSegment(sketch, "E44", {"start": v(-41.79, -168.86) * mm, "end": v(-29.75, -168.86) * mm});
            skLineSegment(sketch, "E45", {"start": v(-23.37, -168.86) * mm, "end": v(-17.35, -168.86) * mm});
            skLineSegment(sketch, "E46", {"start": v(-17.35, -168.86) * mm, "end": v(-17.35, -180.24) * mm});
            skLineSegment(sketch, "E47", {"start": v(-4.18, -180.24) * mm, "end": v(-4.18, -168.86) * mm});
            skLineSegment(sketch, "E48", {"start": v(-4.18, -168.86) * mm, "end": v(1.84, -168.86) * mm});
            skLineSegment(sketch, "E49", {"start": v(8.21, -168.86) * mm, "end": v(20.25, -168.86) * mm});
            skLineSegment(sketch, "E50", {"start": v(26.63, -168.86) * mm, "end": v(32.65, -168.86) * mm});
            skLineSegment(sketch, "E51", {"start": v(32.65, -168.86) * mm, "end": v(32.65, -180.24) * mm});
            skLineSegment(sketch, "E52.trimOffspring", {"start": v(115.82, -332.62) * mm, "end": v(115.82, -346.27) * mm});
            skLineSegment(sketch, "E53.trimOffspring", {"start": v(115.82, -282.67) * mm, "end": v(115.82, -325.12) * mm});
            skLineSegment(sketch, "E54.trimOffspring", {"start": v(115.82, -232.72) * mm, "end": v(115.82, -275.17) * mm});
            skLineSegment(sketch, "E55.trimOffspring", {"start": v(115.82, -182.77) * mm, "end": v(115.82, -225.22) * mm});
            skLineSegment(sketch, "E56.trimOffspring", {"start": v(115.82, -132.82) * mm, "end": v(115.82, -175.27) * mm});
            skLineSegment(sketch, "E57.trimOffspring", {"start": v(115.82, -82.87) * mm, "end": v(115.82, -125.32) * mm});
            skLineSegment(sketch, "E58.trimOffspring", {"start": v(115.82, -32.92) * mm, "end": v(115.82, -75.37) * mm});
            skLineSegment(sketch, "E59.trimOffspring", {"start": v(115.82, 17.03) * mm, "end": v(115.82, -25.42) * mm});
            skLineSegment(sketch, "E60.trimOffspring", {"start": v(115.82, 66.98) * mm, "end": v(115.82, 24.53) * mm});
            skLineSegment(sketch, "E61.trimOffspring", {"start": v(115.82, 116.93) * mm, "end": v(115.82, 74.48) * mm});
            skLineSegment(sketch, "E62.trimOffspring", {"start": v(115.82, 166.88) * mm, "end": v(115.82, 124.43) * mm});
            skLineSegment(sketch, "E63.trimOffspring", {"start": v(115.82, 216.83) * mm, "end": v(115.82, 174.38) * mm});
            skLineSegment(sketch, "E64.trimOffspring", {"start": v(115.82, 266.78) * mm, "end": v(115.82, 224.33) * mm});
            skLineSegment(sketch, "E65.trimOffspring", {"start": v(115.82, 316.73) * mm, "end": v(115.82, 274.28) * mm});
            skLineSegment(sketch, "E66.trimOffspring", {"start": v(115.82, 366.68) * mm, "end": v(115.82, 324.23) * mm});
            skLineSegment(sketch, "E67.trimOffspring", {"start": v(-84.18, -332.62) * mm, "end": v(-84.18, -346.27) * mm});
            skLineSegment(sketch, "E68.trimOffspring", {"start": v(-84.18, -282.67) * mm, "end": v(-84.18, -325.12) * mm});
            skLineSegment(sketch, "E69.trimOffspring", {"start": v(-84.18, -232.72) * mm, "end": v(-84.18, -275.17) * mm});
            skLineSegment(sketch, "E70.trimOffspring", {"start": v(-84.18, -182.77) * mm, "end": v(-84.18, -225.22) * mm});
            skLineSegment(sketch, "E71.trimOffspring", {"start": v(-84.18, -132.82) * mm, "end": v(-84.18, -175.27) * mm});
            skLineSegment(sketch, "E72.trimOffspring", {"start": v(-84.18, -82.87) * mm, "end": v(-84.18, -125.32) * mm});
            skLineSegment(sketch, "E73.trimOffspring", {"start": v(-84.18, -32.92) * mm, "end": v(-84.18, -75.37) * mm});
            skLineSegment(sketch, "E74.trimOffspring", {"start": v(-84.18, 17.03) * mm, "end": v(-84.18, -25.42) * mm});
            skLineSegment(sketch, "E75.trimOffspring", {"start": v(-84.18, 66.98) * mm, "end": v(-84.18, 24.53) * mm});
            skLineSegment(sketch, "E76.trimOffspring", {"start": v(-84.18, 116.93) * mm, "end": v(-84.18, 74.48) * mm});
            skLineSegment(sketch, "E77.trimOffspring", {"start": v(-84.18, 166.88) * mm, "end": v(-84.18, 124.43) * mm});
            skLineSegment(sketch, "E78.trimOffspring", {"start": v(-84.18, 216.83) * mm, "end": v(-84.18, 174.38) * mm});
            skLineSegment(sketch, "E79.trimOffspring", {"start": v(-84.18, 266.78) * mm, "end": v(-84.18, 224.33) * mm});
            skLineSegment(sketch, "E80.trimOffspring", {"start": v(-84.18, 316.73) * mm, "end": v(-84.18, 274.28) * mm});
            skLineSegment(sketch, "E81.trimOffspring", {"start": v(-84.18, 366.68) * mm, "end": v(-84.18, 324.23) * mm});
            skLineSegment(sketch, "E82", {"start": v(-17.35, -134.94) * mm, "end": v(-15.83, -134.94) * mm});
            skLineSegment(sketch, "E83", {"start": v(-35.77, -134.94) * mm, "end": v(-34.24, -134.94) * mm});
            skLineSegment(sketch, "E84", {"start": v(-34.24, -134.94) * mm, "end": v(-33.23, -134.94) * mm});
            skLineSegment(sketch, "E85", {"start": v(14.23, -134.94) * mm, "end": v(15.76, -134.94) * mm});
            skLineSegment(sketch, "E86", {"start": v(16.77, -134.94) * mm, "end": v(15.76, -134.94) * mm});
            skLineSegment(sketch, "E87", {"start": v(32.65, -134.94) * mm, "end": v(34.17, -134.94) * mm});
            skLineSegment(sketch, "E88", {"start": v(-51.64, -284.94) * mm, "end": v(-35.77, -284.94) * mm});
            skLineSegment(sketch, "E89", {"start": v(-35.77, -284.94) * mm, "end": v(-34.24, -284.94) * mm});
            skLineSegment(sketch, "E90", {"start": v(-34.24, -284.94) * mm, "end": v(-33.23, -284.94) * mm});
            skLineSegment(sketch, "E91", {"start": v(15.76, -284.94) * mm, "end": v(16.77, -284.94) * mm});
            skLineSegment(sketch, "E92.0", {"start": v(-52.64, -138) * mm, "end": v(-52.64, -138.87) * mm});
            skLineSegment(sketch, "E93.0", {"start": v(-51.64, -139.37) * mm, "end": v(-32.6, -139.37) * mm});
            skLineSegment(sketch, "E94.0", {"start": v(-33.23, -139.37) * mm, "end": v(-14.18, -139.37) * mm});
            skLineSegment(sketch, "E95.0", {"start": v(-13.18, -138) * mm, "end": v(-13.18, -138.87) * mm});
            skLineSegment(sketch, "E96", {"start": v(-52.64, -138) * mm, "end": v(-51.64, -138) * mm});
            skLineSegment(sketch, "E97", {"start": v(-52.64, -138.87) * mm, "end": v(-52.64, -139.37) * mm});
            skLineSegment(sketch, "E98", {"start": v(-52.64, -139.37) * mm, "end": v(-51.64, -139.37) * mm});
            skLineSegment(sketch, "E99", {"start": v(-14.18, -139.37) * mm, "end": v(-13.18, -139.37) * mm});
            skLineSegment(sketch, "E100", {"start": v(-13.18, -139.37) * mm, "end": v(-13.18, -138.87) * mm});
            skLineSegment(sketch, "E101", {"start": v(-13.18, -138) * mm, "end": v(-14.18, -138) * mm});
            skLineSegment(sketch, "E102.0", {"start": v(-2.64, -138) * mm, "end": v(-2.64, -138.87) * mm});
            skLineSegment(sketch, "E103.0", {"start": v(-1.64, -139.37) * mm, "end": v(17.4, -139.37) * mm});
            skLineSegment(sketch, "E104.0", {"start": v(16.77, -139.37) * mm, "end": v(35.82, -139.37) * mm});
            skLineSegment(sketch, "E105.0", {"start": v(36.82, -138) * mm, "end": v(36.82, -138.87) * mm});
            skLineSegment(sketch, "E106", {"start": v(-2.64, -138) * mm, "end": v(-1.64, -138) * mm});
            skLineSegment(sketch, "E107", {"start": v(-2.64, -138.87) * mm, "end": v(-2.64, -139.37) * mm});
            skLineSegment(sketch, "E108", {"start": v(-2.64, -139.37) * mm, "end": v(-1.64, -139.37) * mm});
            skLineSegment(sketch, "E109", {"start": v(35.82, -139.37) * mm, "end": v(36.82, -139.37) * mm});
            skLineSegment(sketch, "E110", {"start": v(36.82, -139.37) * mm, "end": v(36.82, -138.87) * mm});
            skLineSegment(sketch, "E111", {"start": v(36.82, -138) * mm, "end": v(35.82, -138) * mm});
            skLineSegment(sketch, "E112.0", {"start": v(-52.64, -288) * mm, "end": v(-52.64, -288.87) * mm});
            skLineSegment(sketch, "E113.0", {"start": v(-51.64, -289.37) * mm, "end": v(-32.6, -289.37) * mm});
            skLineSegment(sketch, "E114.0", {"start": v(-33.23, -289.37) * mm, "end": v(-14.18, -289.37) * mm});
            skLineSegment(sketch, "E115.0", {"start": v(-13.18, -288) * mm, "end": v(-13.18, -288.87) * mm});
            skLineSegment(sketch, "E116.0", {"start": v(-2.64, -288) * mm, "end": v(-2.64, -288.87) * mm});
            skLineSegment(sketch, "E117.0", {"start": v(-1.64, -289.37) * mm, "end": v(16.77, -289.37) * mm});
            skLineSegment(sketch, "E118.0", {"start": v(16.77, -289.37) * mm, "end": v(35.82, -289.37) * mm});
            skLineSegment(sketch, "E119.0", {"start": v(36.82, -288) * mm, "end": v(36.82, -288.87) * mm});
            skLineSegment(sketch, "E120", {"start": v(-52.64, -288) * mm, "end": v(-51.64, -288) * mm});
            skLineSegment(sketch, "E121", {"start": v(-52.64, -288.87) * mm, "end": v(-52.64, -289.37) * mm});
            skLineSegment(sketch, "E122", {"start": v(-52.64, -289.37) * mm, "end": v(-51.64, -289.37) * mm});
            skLineSegment(sketch, "E123", {"start": v(-14.18, -289.37) * mm, "end": v(-13.18, -289.37) * mm});
            skLineSegment(sketch, "E124", {"start": v(-13.18, -289.37) * mm, "end": v(-13.18, -288.87) * mm});
            skLineSegment(sketch, "E125", {"start": v(-13.18, -288) * mm, "end": v(-14.18, -288) * mm});
            skLineSegment(sketch, "E126", {"start": v(-2.64, -288) * mm, "end": v(-1.64, -288) * mm});
            skLineSegment(sketch, "E127", {"start": v(-2.64, -288.87) * mm, "end": v(-2.64, -289.37) * mm});
            skLineSegment(sketch, "E128", {"start": v(-2.64, -289.37) * mm, "end": v(-1.64, -289.37) * mm});
            skLineSegment(sketch, "E129", {"start": v(35.82, -289.37) * mm, "end": v(36.82, -289.37) * mm});
            skLineSegment(sketch, "E130", {"start": v(36.82, -289.37) * mm, "end": v(36.82, -288.87) * mm});
            skLineSegment(sketch, "E131", {"start": v(36.82, -288) * mm, "end": v(35.82, -288) * mm});
            skLineSegment(sketch, "E132", {"start": v(-51.64, -138) * mm, "end": v(-54.18, -138) * mm});
            skPoint(sketch, "E132.endSnap0", {"position": v(-52.14, -138) * mm});
            skLineSegment(sketch, "E133", {"start": v(-54.18, -138) * mm, "end": v(-54.18, -132.4) * mm});
            skLineSegment(sketch, "E134", {"start": v(-54.18, -132.4) * mm, "end": v(-14.18, -132.4) * mm});
            skLineSegment(sketch, "E135", {"start": v(-14.18, -132.4) * mm, "end": v(-14.18, -136.59) * mm});
            skLineSegment(sketch, "E136", {"start": v(-4.18, -132.4) * mm, "end": v(-4.18, -138) * mm});
            skPoint(sketch, "E136.endSnap0", {"position": v(-2.14, -138) * mm});
            skLineSegment(sketch, "E137", {"start": v(-4.18, -138) * mm, "end": v(-1.64, -138) * mm});
            skLineSegment(sketch, "E138", {"start": v(-4.18, -132.4) * mm, "end": v(35.82, -132.4) * mm});
            skLineSegment(sketch, "E139", {"start": v(35.82, -132.4) * mm, "end": v(35.82, -136.59) * mm});
            skLineSegment(sketch, "E140", {"start": v(-54.18, -135.2) * mm, "end": v(35.82, -135.2) * mm, "construction": true});
            skLineSegment(sketch, "E141", {"start": v(-54.18, -135.2) * mm, "end": v(-59.18, -135.2) * mm, "construction": true});
            skLineSegment(sketch, "E142", {"start": v(35.82, -135.2) * mm, "end": v(40.82, -135.2) * mm, "construction": true});
            skCircle(sketch, "E143", {"center": v(40.82, -135.2) * mm, "radius": 1.98 * mm});
            skCircle(sketch, "E144", {"center": v(-59.18, -135.2) * mm, "radius": 1.98 * mm});
            skLineSegment(sketch, "E145", {"start": v(-54.18, -282.4) * mm, "end": v(-54.18, -288.87) * mm});
            skLineSegment(sketch, "E146", {"start": v(-54.18, -288.87) * mm, "end": v(-14.18, -288.87) * mm});
            skLineSegment(sketch, "E147", {"start": v(-14.18, -282.4) * mm, "end": v(-14.18, -288.87) * mm});
            skLineSegment(sketch, "E148", {"start": v(-14.18, -282.4) * mm, "end": v(-54.18, -282.4) * mm});
            skLineSegment(sketch, "E149", {"start": v(-4.18, -282.4) * mm, "end": v(35.82, -282.4) * mm});
            skLineSegment(sketch, "E150", {"start": v(35.82, -282.4) * mm, "end": v(35.82, -288) * mm});
            skLineSegment(sketch, "E151", {"start": v(-4.18, -282.4) * mm, "end": v(-4.18, -288.87) * mm});
            skLineSegment(sketch, "E152", {"start": v(-4.18, -288.87) * mm, "end": v(35.82, -288.87) * mm});
            skLineSegment(sketch, "E153", {"start": v(-54.18, -285.63) * mm, "end": v(35.82, -285.63) * mm, "construction": true});
            skPoint(sketch, "E153.endSnap0", {"position": v(35.82, -285.2) * mm});
            skLineSegment(sketch, "E154", {"start": v(35.82, -285.63) * mm, "end": v(40.82, -285.63) * mm, "construction": true});
            skLineSegment(sketch, "E155", {"start": v(-54.18, -285.63) * mm, "end": v(-59.18, -285.63) * mm, "construction": true});
            skCircle(sketch, "E156", {"center": v(-59.18, -285.63) * mm, "radius": 1.75 * mm});
            skCircle(sketch, "E157", {"center": v(40.82, -285.63) * mm, "radius": 1.75 * mm});
            skLineSegment(sketch, "E158", {"start": v(-15.83, -134.94) * mm, "end": v(-14.18, -134.94) * mm});
            skLineSegment(sketch, "E159", {"start": v(-14.18, -134.94) * mm, "end": v(-14.18, -136.59) * mm});
            skLineSegment(sketch, "E160", {"start": v(34.17, -134.94) * mm, "end": v(35.82, -134.94) * mm});
            skPoint(sketch, "E160.endSnap0", {"position": v(35.82, -134.5) * mm});
            skLineSegment(sketch, "E161", {"start": v(35.82, -134.94) * mm, "end": v(35.82, -136.59) * mm});
            skLineSegment(sketch, "E162", {"start": v(-15.83, -284.94) * mm, "end": v(-14.18, -284.94) * mm});
            skPoint(sketch, "E162.endSnap0", {"position": v(-14.18, -285.63) * mm});
            skLineSegment(sketch, "E163", {"start": v(-14.18, -284.94) * mm, "end": v(-14.18, -286.59) * mm});
            skLineSegment(sketch, "E164", {"start": v(34.17, -284.94) * mm, "end": v(35.82, -284.94) * mm});
            skLineSegment(sketch, "E165", {"start": v(35.82, -284.94) * mm, "end": v(35.82, -286.59) * mm});
            skSolve(sketch);
        }
        {
            var Q0;
            Q0=makeQuery(id+"F0.imprint","IMPRINT",FACE,{"disambiguationData":[TD([[makeQuery(id+"F0.imprint","IMPRINT",EDGE,{"derivedFrom":sQuery(id+"F0.wireOp",EDGE,"E0.bottom")}),-1.0]])]});
            extrude(context, id + "F1", {"entities" : qUnion([Q0]), "depth" : 7.5 * mm});
        }
    });
